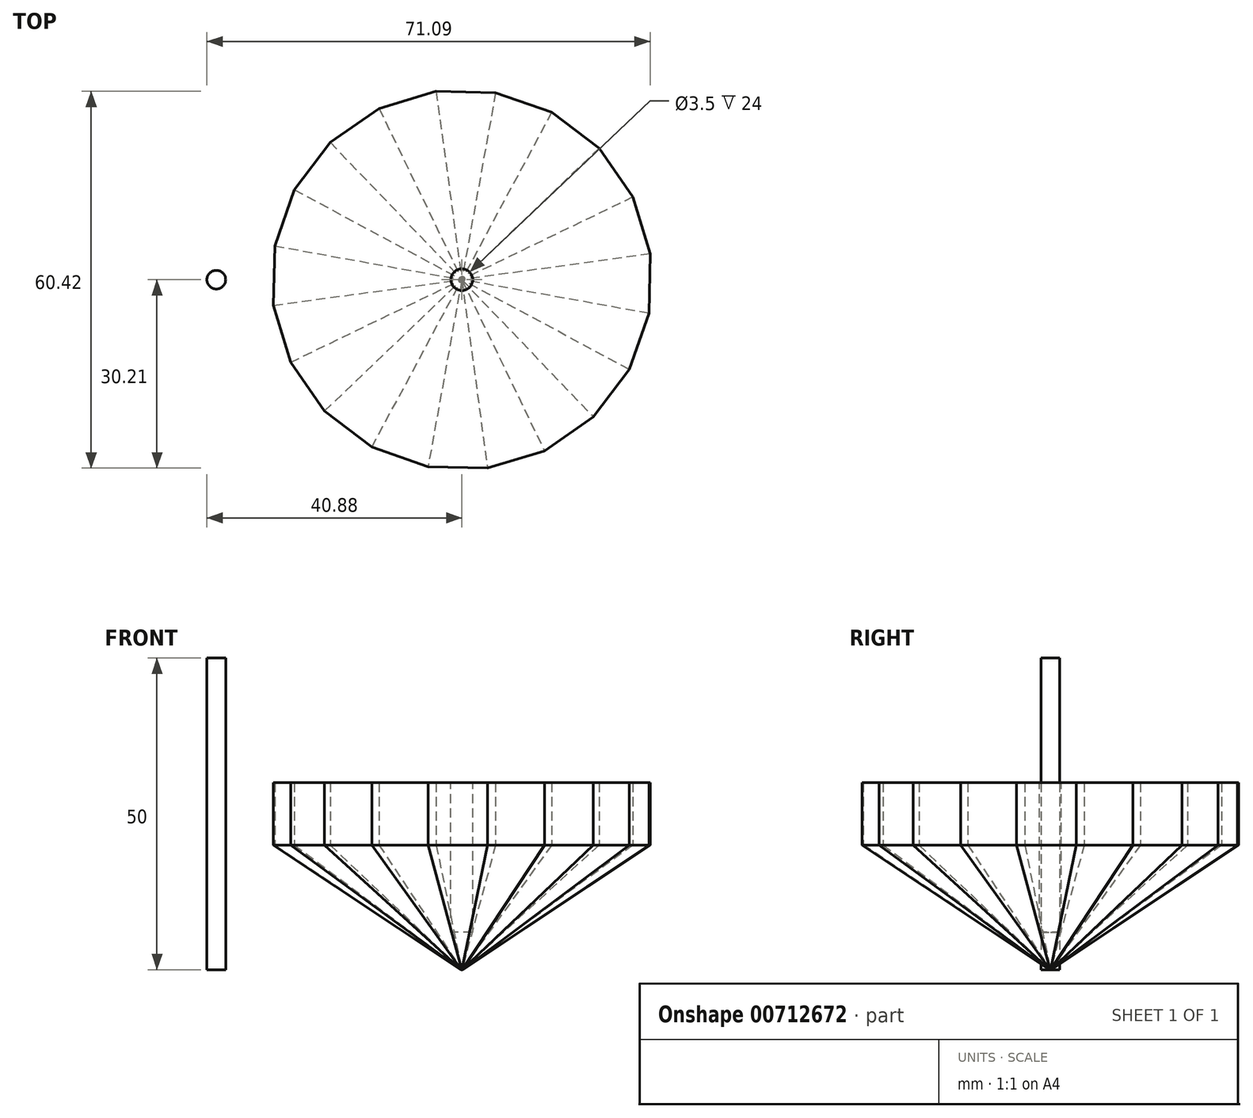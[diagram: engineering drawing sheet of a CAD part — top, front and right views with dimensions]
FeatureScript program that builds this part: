
annotation { "Feature Type Name" : "Feature", "Feature Type Description" : "" }
export const myFeature = defineFeature(function(context is Context, id is Id, definition is map)
    precondition{}
    {
        {
            var Q0;
            Q0=qCreatedBy(makeId("Top.planeOp"),FACE);
            var sketch = newSketch(context, id + "F0", { "sketchPlane" : qUnion([Q0])});
            skCircle(sketch, "E0.cCircle", {"center": v(0, 0) * mm, "radius": 30.1 * mm, "construction": true});
            skLineSegment(sketch, "E0.0", {"start": v(21.09, -22.02) * mm, "end": v(13.25, -27.45) * mm});
            skLineSegment(sketch, "E0.1", {"start": v(13.25, -27.45) * mm, "end": v(4.12, -30.2) * mm});
            skLineSegment(sketch, "E0.2", {"start": v(4.12, -30.2) * mm, "end": v(-5.42, -30) * mm});
            skLineSegment(sketch, "E0.3", {"start": v(-5.42, -30) * mm, "end": v(-14.42, -26.86) * mm});
            skLineSegment(sketch, "E0.4", {"start": v(-14.42, -26.86) * mm, "end": v(-22.02, -21.09) * mm});
            skLineSegment(sketch, "E0.5", {"start": v(-22.02, -21.09) * mm, "end": v(-27.45, -13.25) * mm});
            skLineSegment(sketch, "E0.6", {"start": v(-27.45, -13.25) * mm, "end": v(-30.2, -4.12) * mm});
            skLineSegment(sketch, "E0.7", {"start": v(-30.2, -4.12) * mm, "end": v(-30, 5.42) * mm});
            skLineSegment(sketch, "E0.8", {"start": v(-30, 5.42) * mm, "end": v(-26.86, 14.42) * mm});
            skLineSegment(sketch, "E0.9", {"start": v(-26.86, 14.42) * mm, "end": v(-21.09, 22.02) * mm});
            skLineSegment(sketch, "E0.10", {"start": v(-21.09, 22.02) * mm, "end": v(-13.25, 27.45) * mm});
            skLineSegment(sketch, "E0.11", {"start": v(-13.25, 27.45) * mm, "end": v(-4.12, 30.2) * mm});
            skLineSegment(sketch, "E0.12", {"start": v(-4.12, 30.2) * mm, "end": v(5.42, 30) * mm});
            skLineSegment(sketch, "E0.13", {"start": v(5.42, 30) * mm, "end": v(14.42, 26.86) * mm});
            skLineSegment(sketch, "E0.14", {"start": v(14.42, 26.86) * mm, "end": v(22.02, 21.09) * mm});
            skLineSegment(sketch, "E0.15", {"start": v(22.02, 21.09) * mm, "end": v(27.45, 13.25) * mm});
            skLineSegment(sketch, "E0.16", {"start": v(27.45, 13.25) * mm, "end": v(30.2, 4.12) * mm});
            skLineSegment(sketch, "E0.17", {"start": v(30.2, 4.12) * mm, "end": v(30, -5.42) * mm});
            skLineSegment(sketch, "E0.18", {"start": v(30, -5.42) * mm, "end": v(26.86, -14.42) * mm});
            skLineSegment(sketch, "E0.19", {"start": v(26.86, -14.42) * mm, "end": v(21.09, -22.02) * mm});
            skPoint(sketch, "E0.0.midPoint", {"position": v(17.17, -24.74) * mm});
            skSolve(sketch);
        }
        {
            var Q0;
            Q0=makeQuery(id+"F0.imprint","IMPRINT",FACE,{"disambiguationData":[TD([[makeQuery(id+"F0.imprint","IMPRINT",EDGE,{"derivedFrom":sQuery(id+"F0.wireOp",EDGE,"E0.0")}),-1.0]])]});
            extrude(context, id + "F1", {"entities" : qUnion([Q0]), "depth" : 30 * mm, "offsetDistance" : 25 * mm});
        }
        {
            var Q0;
            Q0=makeQuery(id+"F1.opExtrude","CAP_EDGE",EDGE,{"disambiguationData":[OSD([sQuery(id+"F0.wireOp",EDGE,"E0.3")])],"isStart":true});
            var Q1;
            Q1=makeQuery(id+"F1.opExtrude","CAP_EDGE",EDGE,{"disambiguationData":[OSD([sQuery(id+"F0.wireOp",EDGE,"E0.2")])],"isStart":true});
            var Q2;
            Q2=makeQuery(id+"F1.opExtrude","CAP_EDGE",EDGE,{"disambiguationData":[OSD([sQuery(id+"F0.wireOp",EDGE,"E0.1")])],"isStart":true});
            var Q3;
            Q3=makeQuery(id+"F1.opExtrude","CAP_FACE",FACE,{"disambiguationData":[OSD([sQuery(id+"F0.wireOp",EDGE,"E0.0"),sQuery(id+"F0.wireOp",EDGE,"E0.1"),sQuery(id+"F0.wireOp",EDGE,"E0.2"),sQuery(id+"F0.wireOp",EDGE,"E0.3"),sQuery(id+"F0.wireOp",EDGE,"E0.4"),sQuery(id+"F0.wireOp",EDGE,"E0.5"),sQuery(id+"F0.wireOp",EDGE,"E0.6"),sQuery(id+"F0.wireOp",EDGE,"E0.7"),sQuery(id+"F0.wireOp",EDGE,"E0.8"),sQuery(id+"F0.wireOp",EDGE,"E0.9"),sQuery(id+"F0.wireOp",EDGE,"E0.10"),sQuery(id+"F0.wireOp",EDGE,"E0.11"),sQuery(id+"F0.wireOp",EDGE,"E0.12"),sQuery(id+"F0.wireOp",EDGE,"E0.13"),sQuery(id+"F0.wireOp",EDGE,"E0.14"),sQuery(id+"F0.wireOp",EDGE,"E0.15"),sQuery(id+"F0.wireOp",EDGE,"E0.16"),sQuery(id+"F0.wireOp",EDGE,"E0.17"),sQuery(id+"F0.wireOp",EDGE,"E0.18"),sQuery(id+"F0.wireOp",EDGE,"E0.19")])],"isStart":true});
            chamfer(context, id + "F2", {"entities" : qUnion([Q0, Q1, Q2, Q3]), "chamferType" : ChamferType.TWO_OFFSETS, "width1" : 30 * mm, "oppositeDirection" : false, "width2" : 20 * mm, "tangentPropagation" : true});
        }
        {
            var Q0;
            Q0=makeQuery(id+"F1.opExtrude","CAP_FACE",FACE,{"disambiguationData":[OSD([sQuery(id+"F0.wireOp",EDGE,"E0.0"),sQuery(id+"F0.wireOp",EDGE,"E0.1"),sQuery(id+"F0.wireOp",EDGE,"E0.2"),sQuery(id+"F0.wireOp",EDGE,"E0.3"),sQuery(id+"F0.wireOp",EDGE,"E0.4"),sQuery(id+"F0.wireOp",EDGE,"E0.5"),sQuery(id+"F0.wireOp",EDGE,"E0.6"),sQuery(id+"F0.wireOp",EDGE,"E0.7"),sQuery(id+"F0.wireOp",EDGE,"E0.8"),sQuery(id+"F0.wireOp",EDGE,"E0.9"),sQuery(id+"F0.wireOp",EDGE,"E0.10"),sQuery(id+"F0.wireOp",EDGE,"E0.11"),sQuery(id+"F0.wireOp",EDGE,"E0.12"),sQuery(id+"F0.wireOp",EDGE,"E0.13"),sQuery(id+"F0.wireOp",EDGE,"E0.14"),sQuery(id+"F0.wireOp",EDGE,"E0.15"),sQuery(id+"F0.wireOp",EDGE,"E0.16"),sQuery(id+"F0.wireOp",EDGE,"E0.17"),sQuery(id+"F0.wireOp",EDGE,"E0.18"),sQuery(id+"F0.wireOp",EDGE,"E0.19")])],"isStart":false});
            var sketch = newSketch(context, id + "F3", { "sketchPlane" : qUnion([Q0])});
            skCircle(sketch, "E1", {"center": v(0, 0) * mm, "radius": 1.75 * mm});
            skSolve(sketch);
        }
        {
            var Q0;
            Q0=makeQuery(id+"F3.imprint","IMPRINT",FACE,{"disambiguationData":[TD([[makeQuery(id+"F3.imprint","IMPRINT",EDGE,{"derivedFrom":sQuery(id+"F3.wireOp",EDGE,"E1")}),1.0]])]});
            extrude(context, id + "F4", {"entities" : qUnion([Q0]), "operationType" : NewBodyOperationType.REMOVE, "oppositeDirection" : true, "depth" : 24 * mm, "offsetDistance" : 25 * mm});
        }
        {
            var Q0;
            Q0=qCreatedBy(makeId("Top.planeOp"),FACE);
            var sketch = newSketch(context, id + "F5", { "sketchPlane" : qUnion([Q0])});
            skCircle(sketch, "E2", {"center": v(-39.38, 0) * mm, "radius": 1.5 * mm});
            skSolve(sketch);
        }
        {
            var Q0;
            Q0=makeQuery(id+"F5.imprint","IMPRINT",FACE,{"disambiguationData":[TD([[makeQuery(id+"F5.imprint","IMPRINT",EDGE,{"derivedFrom":sQuery(id+"F5.wireOp",EDGE,"E2")}),1.0]])]});
            var Q1;
            Q1=sQuery(id+"F5.wireOp",EDGE,"E2");
            extrude(context, id + "F6", {"entities" : qUnion([Q0]), "surfaceEntities" : qUnion([Q1]), "depth" : 50 * mm, "offsetDistance" : 25 * mm});
        }
    });
